# Revit family: ML-820 BI
name_source: partatom
category: Specialty Equipment
revit_build: Autodesk Revit 2017 (Build: 20160225_1515(x64)
units: mm (PartAtom-declared; Revit-internal decimal feet)

## family parameters
Always vertical = Yes
Cut with Voids When Loaded = No
OmniClass Number = 23.75.00.00
OmniClass Title = Climate Control (HVAC)
Part Type = Normal
Room Calculation Point = No
Round Connector Dimension = Use Diameter
Shared = No
Work Plane-Based = No

## types (1)
- ML 820 BI
    Borde Aluminio = Teka_Acero Inox
    Ca_1_Cable de conexión = 0 mm  [stored 0 ft]
    Ca_1_Frecuencia Hz. = 50
    Ca_1_Potencia grill W. = -
    Ca_1_Potencia nominal max. W. = 1100
    Ca_1_Potencia salida mwo W. = 700
    Ca_1_Potencia turbo W. = -
    Ca_1_Tensión 220/240 V. = SI
    Ca_2_Acabado Slim en acero inox antihuella = Yes
    Ca_2_Base Cerámica = No
    Ca_2_Botón + 1 minuto = No
    Ca_2_Botón + 30 segundos = No
    Ca_2_Descongelación por peso = No
    Ca_2_Descongelación por tiempo = Yes
    Ca_2_Funciones de cocinado = 1
    Ca_2_Grill Abatible = No
    Ca_2_Interior cavidad = Inox
    Ca_2_Marco de acero inox. opcional = No
    Ca_2_Menus de cocción directa = 1
    Ca_2_Microondas + Grill = No
    Ca_2_Niveles de potencia = 5
    Ca_2_Panel de mandos Touch Control = Yes
    Ca_2_Panel de mandos electromecánico = Yes
    Ca_2_Panel de mandos electrónico = No
    Ca_2_Plato giratorio integrado = Yes
    Ca_2_Temporizador (minutos) = 60
    Ca_2_Tipo de instalación = Integración
    Ca_3_Bloqueo de seguridad del panel = No
    Ca_3_Grill de cuarzo integrado = No
    Ca_3_Grill de resistencia = No
    Ca_3_Puerta con chip de seguridad = Yes
    Ca_3_Termostato de Seguridad = Yes
    Ca_3_Ventilación de enfriamiento = Yes
    Ca_4_Parrilla para cocinado = No
    Ca_4_Plato dorador = No
    Ca_Alto = 390 mm
    Ca_Alto Interior = 210 mm
    Ca_Ancho = 595 mm
    Ca_Ancho Interior = 305 mm
    Ca_Capacidad en Litros = 20
    Ca_Creado por = Catálogo Arquitectura
    Ca_Código Catálogo Arquitectura = 465_TEK_014
    Ca_Código EAN = 8421152145562
    Ca_Código del Producto = 40584201
    Ca_Especificaciones Técnicas = Microondas empotrable para cocina modelo ML 820 BI
    Ca_Fabricante = Teka
    Ca_Instalación = Empotrado
    Ca_Itemizado CDT = E 08 06 02
    Ca_Masterformat = 11 30 13.13
    Ca_Material Principal = Acero inoxidable antihuella
    Ca_Medidas de embalaje = 450 x 645 x 440 mm
    Ca_País de Fabricación = Portugal
    Ca_Peso = 21,5 kg
    Ca_Producto = Microondas ML 820 BI
    Ca_Profundidad = 325 mm
    Ca_Profundidad Interior = 280 mm
    Ca_Representante = Teka
    Ca_Teléfono = 99821 1017
    Ca_Usos = Microondas empotrable para muebles de cocina
    Ca_Web del Fabricante = www.teka.com
    Ca_Web del Representante = www.teka.cl
    Description = Microondas empotrable para muebles de cocina
    Interior Negro = Teka_Interior Negro
    Logo Teka = Teka_Logo
    Manufacturer = Teka
    Model = ML 820 BI
    Panel Interior = Teka_Panel Interior
    Panel Negro = Teka_Panel Negro
    Panel Vidrio = Teka_Panel Vidrio
    Perilla Aluminio = Teka_Acero Inox
    Perilla Negro = Teka_Perilla Negro
    URL = www.teka.cl

note: [stored X ft] marks values corroborated as IEEE doubles in the binary element streams (Revit-internal decimal feet)
